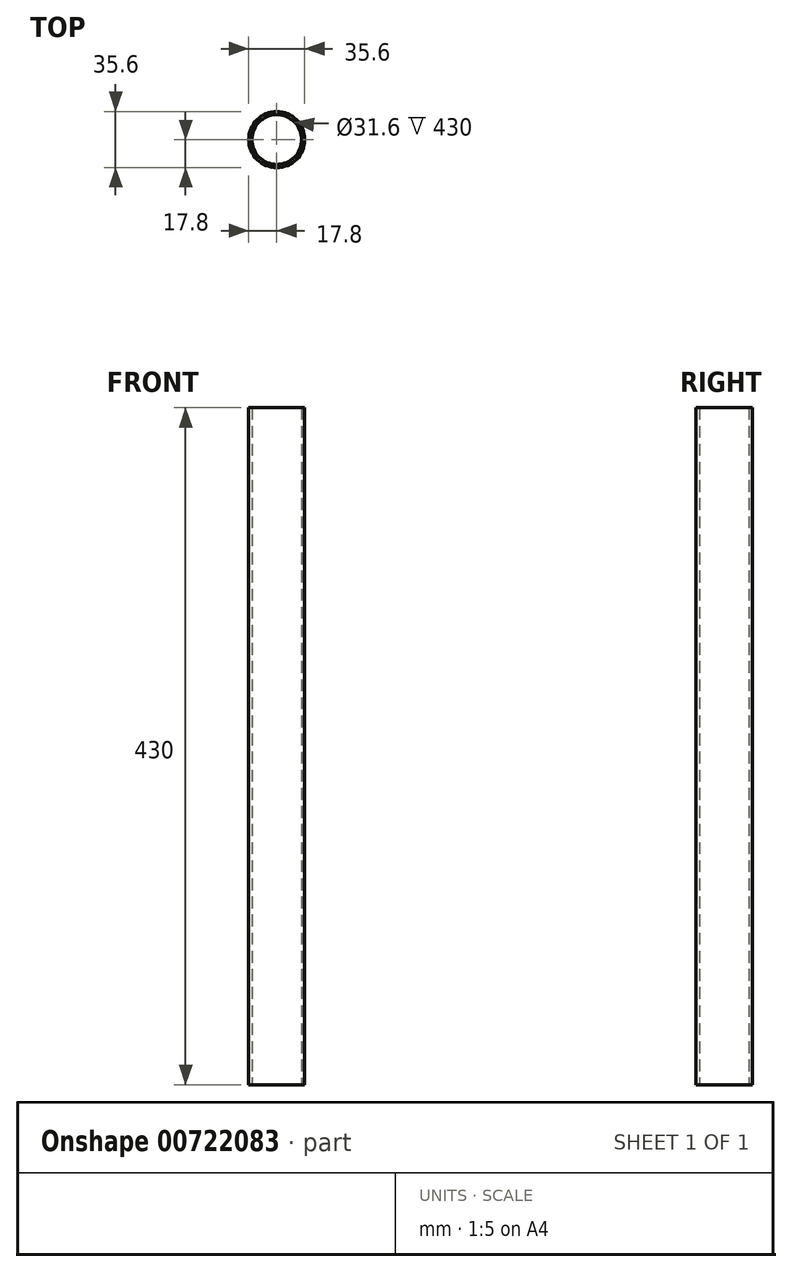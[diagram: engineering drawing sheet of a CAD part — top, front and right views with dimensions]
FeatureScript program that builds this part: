
annotation { "Feature Type Name" : "Feature", "Feature Type Description" : "" }
export const myFeature = defineFeature(function(context is Context, id is Id, definition is map)
    precondition{}
    {
        {
            var Q0;
            Q0=qCreatedBy(makeId("Top.planeOp"),FACE);
            var sketch = newSketch(context, id + "F0", { "sketchPlane" : qUnion([Q0])});
            skCircle(sketch, "E0", {"center": v(0, 0) * mm, "radius": 17.8 * mm});
            skCircle(sketch, "E1", {"center": v(0, 0) * mm, "radius": 15.8 * mm});
            skSolve(sketch);
        }
        {
            var Q0;
            Q0 = qSketchRegion(id + "F0", true);
            extrude(context, id + "F1", {"entities" : qUnion([Q0]), "depth" : 430 * mm, "offsetDistance" : 25 * mm});
        }
    });
